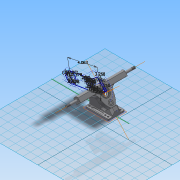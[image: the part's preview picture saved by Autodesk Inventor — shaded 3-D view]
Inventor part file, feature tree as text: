
AUTODESK INVENTOR PART (.ipt)
format: ipt  version: 2014 SP2 (Build 180246200, 246)  size: 531,456 bytes
history: native  units: in
note: dims shown in document units (in); Inventor stores cm internally (conversion verified against a paired STEP export)
features: other x12, sketch x1
ambient origin geometry x8: Origin, YZ Plane, XZ Plane, XY Plane, X Axis, Y Axis, Z Axis, Center Point
bodies: Solid1 (feature_tree), Solid2 (feature_tree)
feature tree (13):
  other  "Truck Caliber50 9in.iam"
  other  "Baseplate Caliber50 9in.ipt:1"
  other  "Hanger Caliber50 9in.ipt:1"
  other  "Axle Centers"
  other  "Parts"
  other  "Work Axis1"
  other  "Work Axis2"
  other  "Work Axis3"
  other  "Work Axis1_1"
  other  "Work Axis2_1"
  other  "Work Axis3_1"
  other  "Work Point1"
  sketch  "Sketch1_1"  dims[d0=0.3937in d2=3.2677in d3=0.2756in d4=1.9291in d5=4.0625in d9=0.4921in d10=1.5748in d12=360.0deg d14=0.25in d15=0.25in d19=0.1065in d20=0.1065in d21=0.25in d22=0.1065in d23=0.1065in d24=0.25in d25=0.1065in d26=0.1065in d27=0.25in d28=0.1065in d29=0.1065in d30=0.0312in d32=1.378in d34=0.25in d35=0.1065in d36=0.1065in d38=0.25in d40=0.25in d41=0.1065in d42=0.1065in d46=0.5in d47=0.25in d48=0.25in d49=0.1065in d50=0.1065in d51=0.25in d52=0.25in d53=0.25in d54=0.1065in d55=0.1065in d56=0.25in d57=0.25in d58=0.25in d59=0.25in d61=0.25in d64=0.0312in d65=0.25in d66=0.25in d67=0.8in]
